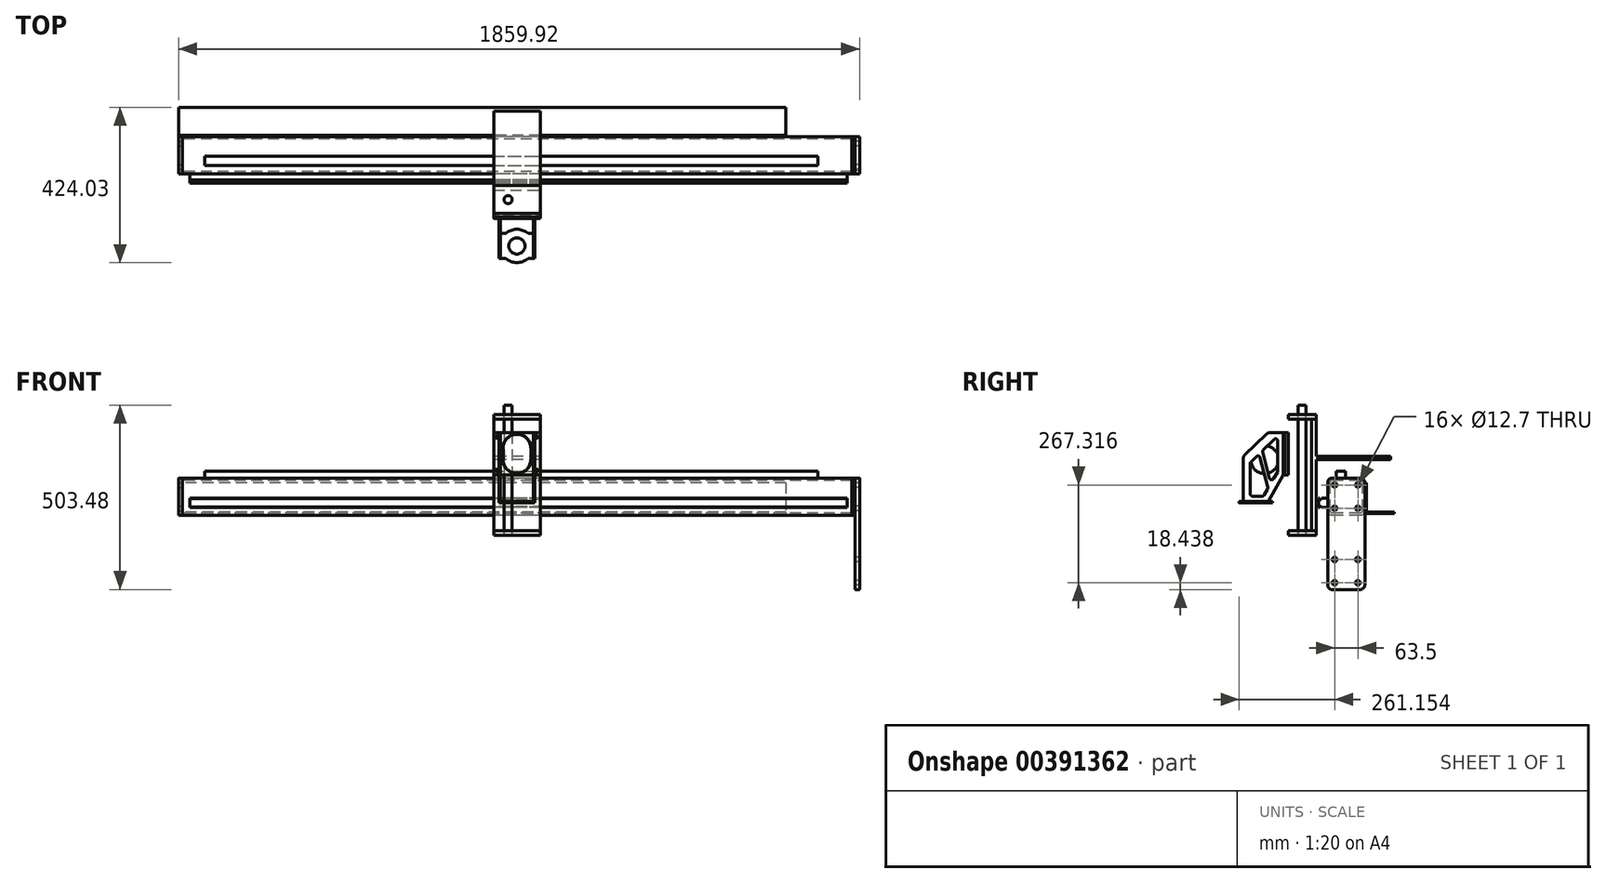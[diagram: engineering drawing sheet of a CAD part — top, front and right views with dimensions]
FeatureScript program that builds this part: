
annotation { "Feature Type Name" : "Feature", "Feature Type Description" : "" }
export const myFeature = defineFeature(function(context is Context, id is Id, definition is map)
    precondition{}
    {
        {
            var Q0;
            Q0=qCreatedBy(makeId("Right.planeOp"),FACE);
            var sketch = newSketch(context, id + "F0", { "sketchPlane" : qUnion([Q0])});
            skLineSegment(sketch, "E0.bottom", {"start": v(127.06, -109.78) * mm, "end": v(50.86, -109.78) * mm});
            skLineSegment(sketch, "E0.top", {"start": v(127.06, -8.18) * mm, "end": v(50.86, -8.18) * mm});
            skLineSegment(sketch, "E0.left", {"start": v(139.76, -97.08) * mm, "end": v(139.76, -20.88) * mm});
            skLineSegment(sketch, "E0.right", {"start": v(38.16, -97.08) * mm, "end": v(38.16, -20.88) * mm});
            skPoint(sketch, "E0.middle", {"position": v(88.96, -58.98) * mm});
            skPoint(sketch, "E1.visualSharp", {"position": v(38.16, -8.18) * mm});
            skArc(sketch, "E1.filletArc", {"start": v(50.86, -8.18) * mm, "mid": v(41.88, -11.9) * mm, "end": v(38.16, -20.88) * mm});
            skPoint(sketch, "E2.visualSharp", {"position": v(139.76, -8.18) * mm});
            skArc(sketch, "E2.filletArc", {"start": v(139.76, -20.88) * mm, "mid": v(136.04, -11.9) * mm, "end": v(127.06, -8.18) * mm});
            skPoint(sketch, "E3.visualSharp", {"position": v(139.76, -109.78) * mm});
            skArc(sketch, "E3.filletArc", {"start": v(127.06, -109.78) * mm, "mid": v(136.04, -106.06) * mm, "end": v(139.76, -97.08) * mm});
            skPoint(sketch, "E4.visualSharp", {"position": v(38.16, -109.78) * mm});
            skArc(sketch, "E4.filletArc", {"start": v(38.16, -97.08) * mm, "mid": v(41.88, -106.06) * mm, "end": v(50.86, -109.78) * mm});
            skArc(sketch, "E5.0", {"start": v(44.51, -97.08) * mm, "mid": v(46.37, -101.57) * mm, "end": v(50.86, -103.43) * mm});
            skLineSegment(sketch, "E5.1", {"start": v(127.06, -103.43) * mm, "end": v(50.86, -103.43) * mm});
            skLineSegment(sketch, "E5.2", {"start": v(44.51, -97.08) * mm, "end": v(44.51, -20.88) * mm});
            skArc(sketch, "E5.3", {"start": v(127.06, -103.43) * mm, "mid": v(131.55, -101.57) * mm, "end": v(133.41, -97.08) * mm});
            skArc(sketch, "E5.4", {"start": v(50.86, -14.53) * mm, "mid": v(46.37, -16.39) * mm, "end": v(44.51, -20.88) * mm});
            skLineSegment(sketch, "E5.5", {"start": v(127.06, -14.53) * mm, "end": v(50.86, -14.53) * mm});
            skArc(sketch, "E5.6", {"start": v(133.41, -20.88) * mm, "mid": v(131.55, -16.39) * mm, "end": v(127.06, -14.53) * mm});
            skLineSegment(sketch, "E5.7", {"start": v(133.41, -97.08) * mm, "end": v(133.41, -20.88) * mm});
            skSolve(sketch);
        }
        {
            var Q0;
            Q0=qCreatedBy(makeId("Top.planeOp"),FACE);
            var sketch = newSketch(context, id + "F1", { "sketchPlane" : qUnion([Q0])});
            skLineSegment(sketch, "E6.bottom", {"start": v(-63.5, -6.35) * mm, "end": v(63.5, -6.35) * mm});
            skLineSegment(sketch, "E6.top", {"start": v(-63.5, 6.35) * mm, "end": v(63.5, 6.35) * mm});
            skLineSegment(sketch, "E6.left", {"start": v(-63.5, -6.35) * mm, "end": v(-63.5, 6.35) * mm});
            skLineSegment(sketch, "E6.right", {"start": v(63.5, -6.35) * mm, "end": v(63.5, 6.35) * mm});
            skPoint(sketch, "E6.middle", {"position": v(0, 0) * mm});
            skSolve(sketch);
        }
        {
            var Q0;
            Q0 = qSketchRegion(id + "F1", true);
            extrude(context, id + "F2", {"entities" : qUnion([Q0]), "depth" : 304.8 * mm, "offsetDistance" : 25.4 * mm, "symmetric" : true});
        }
        {
            var Q0;
            Q0=makeQuery(id+"F2.opExtrude","CAP_FACE",FACE,{"disambiguationData":[OSD([sQuery(id+"F1.wireOp",EDGE,"E6.bottom"),sQuery(id+"F1.wireOp",EDGE,"E6.top"),sQuery(id+"F1.wireOp",EDGE,"E6.left"),sQuery(id+"F1.wireOp",EDGE,"E6.right")])],"isStart":false});
            var sketch = newSketch(context, id + "F3", { "sketchPlane" : qUnion([Q0])});
            skLineSegment(sketch, "E7.bottom", {"start": v(-63.5, 6.35) * mm, "end": v(63.5, 6.35) * mm});
            skLineSegment(sketch, "E7.top", {"start": v(-63.5, -69.85) * mm, "end": v(63.5, -69.85) * mm});
            skLineSegment(sketch, "E7.left", {"start": v(-63.5, 6.35) * mm, "end": v(-63.5, -69.85) * mm});
            skLineSegment(sketch, "E7.right", {"start": v(63.5, 6.35) * mm, "end": v(63.5, -69.85) * mm});
            skSolve(sketch);
        }
        {
            var Q0;
            Q0 = qSketchRegion(id + "F3", true);
            extrude(context, id + "F4", {"entities" : qUnion([Q0]), "depth" : 12.7 * mm, "offsetDistance" : 25.4 * mm});
        }
        {
            var Q0;
            Q0=makeQuery(id+"F2.opExtrude","CAP_FACE",FACE,{"disambiguationData":[OSD([sQuery(id+"F1.wireOp",EDGE,"E6.bottom"),sQuery(id+"F1.wireOp",EDGE,"E6.top"),sQuery(id+"F1.wireOp",EDGE,"E6.left"),sQuery(id+"F1.wireOp",EDGE,"E6.right")])],"isStart":true});
            var sketch = newSketch(context, id + "F5", { "sketchPlane" : qUnion([Q0])});
            skLineSegment(sketch, "E8.bottom", {"start": v(-63.5, -6.35) * mm, "end": v(63.5, -6.35) * mm});
            skLineSegment(sketch, "E8.top", {"start": v(-63.5, 69.85) * mm, "end": v(63.5, 69.85) * mm});
            skLineSegment(sketch, "E8.left", {"start": v(-63.5, -6.35) * mm, "end": v(-63.5, 69.85) * mm});
            skLineSegment(sketch, "E8.right", {"start": v(63.5, -6.35) * mm, "end": v(63.5, 69.85) * mm});
            skSolve(sketch);
        }
        {
            var Q0;
            {var subQ0=sQuery(id+"F5.wireOp",EDGE,"E8.top");Q0=makeQuery(id+"F5.imprint","IMPRINT",FACE,{"disambiguationData":[TD([[makeQuery(id+"F5.imprint","IMPRINT",EDGE,{"derivedFrom":subQ0}),-1.0]])]});}
            var Q1;
            {var subQ0=sQuery(id+"F5.wireOp",EDGE,"E8.bottom");Q1=makeQuery(id+"F5.imprint","IMPRINT",FACE,{"disambiguationData":[TD([[makeQuery(id+"F5.imprint","IMPRINT",EDGE,{"derivedFrom":subQ0}),1.0]])]});}
            extrude(context, id + "F6", {"entities" : qUnion([Q0, Q1]), "depth" : 12.7 * mm, "offsetDistance" : 25.4 * mm});
        }
        {
            var Q0;
            Q0=makeQuery(id+"F4.opExtrude","CAP_FACE",FACE,{"disambiguationData":[OSD([sQuery(id+"F3.wireOp",EDGE,"E7.bottom"),sQuery(id+"F3.wireOp",EDGE,"E7.top"),sQuery(id+"F3.wireOp",EDGE,"E7.left"),sQuery(id+"F3.wireOp",EDGE,"E7.right")])],"isStart":false});
            var sketch = newSketch(context, id + "F7", { "sketchPlane" : qUnion([Q0])});
            skCircle(sketch, "E9", {"center": v(-24.05, -31.75) * mm, "radius": 11.11 * mm});
            skPoint(sketch, "E9.centerSnap0", {"position": v(-63.5, -31.75) * mm});
            skSolve(sketch);
        }
        {
            var Q0;
            Q0 = qSketchRegion(id + "F7", true);
            extrude(context, id + "F8", {"entities" : qUnion([Q0]), "operationType" : NewBodyOperationType.REMOVE, "endBound" : BoundingType.THROUGH_ALL, "oppositeDirection" : true, "depth" : 25.4 * mm, "offsetDistance" : 25.4 * mm});
        }
        {
            var Q0;
            Q0=makeQuery(id+"F7.imprint","IMPRINT",FACE,{"disambiguationData":[TD([[makeQuery(id+"F7.imprint","IMPRINT",EDGE,{"derivedFrom":sQuery(id+"F7.wireOp",EDGE,"E9")}),1.0]])]});
            extrude(context, id + "F9", {"entities" : qUnion([Q0]), "depth" : 25.4 * mm, "offsetDistance" : 25.4 * mm, "hasSecondDirection" : true, "secondDirectionOppositeDirection" : true, "secondDirectionDepth" : 329.7 * mm});
        }
        {
            var Q0;
            Q0=makeQuery(id+"F4.opExtrude","SWEPT_FACE",FACE,{"disambiguationData":[OSD([sQuery(id+"F3.wireOp",EDGE,"E7.top")])]});
            var sketch = newSketch(context, id + "F10", { "sketchPlane" : qUnion([Q0])});
            skLineSegment(sketch, "E10.bottom", {"start": v(-63.5, 115.31) * mm, "end": v(63.5, 115.31) * mm});
            skLineSegment(sketch, "E10.top", {"start": v(-63.5, 0) * mm, "end": v(63.5, 0) * mm});
            skLineSegment(sketch, "E10.left", {"start": v(-63.5, 115.31) * mm, "end": v(-63.5, 0) * mm});
            skLineSegment(sketch, "E10.right", {"start": v(63.5, 115.31) * mm, "end": v(63.5, 0) * mm});
            skSolve(sketch);
        }
        {
            var Q0;
            Q0 = qSketchRegion(id + "F10", true);
            extrude(context, id + "F11", {"entities" : qUnion([Q0]), "depth" : 9.52 * mm, "offsetDistance" : 25.4 * mm});
        }
        {
            var Q0;
            Q0=makeQuery(id+"F11.opExtrude","CAP_FACE",FACE,{"disambiguationData":[OSD([sQuery(id+"F10.wireOp",EDGE,"E10.bottom"),sQuery(id+"F10.wireOp",EDGE,"E10.top"),sQuery(id+"F10.wireOp",EDGE,"E10.left"),sQuery(id+"F10.wireOp",EDGE,"E10.right")])],"isStart":false});
            var sketch = newSketch(context, id + "F12", { "sketchPlane" : qUnion([Q0])});
            skLineSegment(sketch, "E11", {"start": v(0, 72.63) * mm, "end": v(0, 42.69) * mm});
            skPoint(sketch, "E12", {"position": v(0, 57.66) * mm});
            skArc(sketch, "E13.0.startCap", {"start": v(-38.1, 72.63) * mm, "mid": v(0, 110.73) * mm, "end": v(38.1, 72.63) * mm});
            skArc(sketch, "E13.0.endCap", {"start": v(38.1, 42.69) * mm, "mid": v(0, 4.59) * mm, "end": v(-38.1, 42.69) * mm});
            skLineSegment(sketch, "E13.0.left", {"start": v(38.1, 72.63) * mm, "end": v(38.1, 42.69) * mm});
            skLineSegment(sketch, "E13.0.right", {"start": v(-38.1, 72.63) * mm, "end": v(-38.1, 42.69) * mm});
            skSolve(sketch);
        }
        {
            var Q0;
            Q0 = qSketchRegion(id + "F12", true);
            extrude(context, id + "F13", {"entities" : qUnion([Q0]), "operationType" : NewBodyOperationType.REMOVE, "oppositeDirection" : true, "depth" : 3.17 * mm, "offsetDistance" : 25.4 * mm});
        }
        {
            var Q0;
            Q0=makeQuery(id+"F11.opExtrude","CAP_FACE",FACE,{"disambiguationData":[OSD([sQuery(id+"F10.wireOp",EDGE,"E10.bottom"),sQuery(id+"F10.wireOp",EDGE,"E10.top"),sQuery(id+"F10.wireOp",EDGE,"E10.left"),sQuery(id+"F10.wireOp",EDGE,"E10.right")])],"isStart":false});
            var sketch = newSketch(context, id + "F14", { "sketchPlane" : qUnion([Q0])});
            skCircle(sketch, "E14", {"center": v(-55.13, 103.66) * mm, "radius": 3.18 * mm});
            skCircle(sketch, "E15", {"center": v(-55.13, 12.54) * mm, "radius": 3.18 * mm});
            skLineSegment(sketch, "E16", {"start": v(0, 115.31) * mm, "end": v(0, 0) * mm, "construction": true});
            skCircle(sketch, "E17.MirrorC", {"center": v(55.13, 103.66) * mm, "radius": 3.18 * mm});
            skCircle(sketch, "E18.MirrorC", {"center": v(55.13, 12.54) * mm, "radius": 3.18 * mm});
            skSolve(sketch);
        }
        {
            var Q0;
            Q0 = qSketchRegion(id + "F14", true);
            extrude(context, id + "F15", {"entities" : qUnion([Q0]), "operationType" : NewBodyOperationType.REMOVE, "oppositeDirection" : true, "depth" : 4.75 * mm, "offsetDistance" : 25.4 * mm});
        }
        {
            var Q0;
            Q0=makeQuery(id+"F11.opExtrude","CAP_FACE",FACE,{"disambiguationData":[OSD([sQuery(id+"F10.wireOp",EDGE,"E10.bottom"),sQuery(id+"F10.wireOp",EDGE,"E10.top"),sQuery(id+"F10.wireOp",EDGE,"E10.left"),sQuery(id+"F10.wireOp",EDGE,"E10.right")])],"isStart":false});
            var sketch = newSketch(context, id + "F16", { "sketchPlane" : qUnion([Q0])});
            skLineSegment(sketch, "E19.bottom", {"start": v(-61.01, 115.31) * mm, "end": v(0, 115.31) * mm});
            skLineSegment(sketch, "E19.top", {"start": v(-61.01, 0) * mm, "end": v(0, 0) * mm});
            skLineSegment(sketch, "E19.left", {"start": v(-63.5, 112.83) * mm, "end": v(-63.5, 2.49) * mm});
            skCircle(sketch, "E20.0", {"center": v(-55.13, 103.66) * mm, "radius": 3.17 * mm});
            skCircle(sketch, "E20.1", {"center": v(-55.13, 12.54) * mm, "radius": 3.17 * mm});
            skPoint(sketch, "E21.visualSharp", {"position": v(-44.45, 0) * mm});
            skPoint(sketch, "E22.visualSharp", {"position": v(-44.45, 115.31) * mm});
            skPoint(sketch, "E23.visualSharp", {"position": v(-63.5, 115.31) * mm});
            skArc(sketch, "E23.filletArc", {"start": v(-61.01, 115.31) * mm, "mid": v(-62.77, 114.58) * mm, "end": v(-63.5, 112.83) * mm});
            skPoint(sketch, "E24.visualSharp", {"position": v(-63.5, 0) * mm});
            skArc(sketch, "E24.filletArc", {"start": v(-63.5, 2.49) * mm, "mid": v(-62.77, 0.73) * mm, "end": v(-61.01, 0) * mm});
            skLineSegment(sketch, "E25", {"start": v(0, 115.31) * mm, "end": v(0, 0) * mm, "construction": true});
            skArc(sketch, "E26.MirrorCS", {"start": v(63.5, 2.49) * mm, "mid": v(62.77, 0.73) * mm, "end": v(61.01, 0) * mm});
            skArc(sketch, "E27.MirrorCS", {"start": v(61.01, 115.31) * mm, "mid": v(62.77, 114.58) * mm, "end": v(63.5, 112.83) * mm});
            skCircle(sketch, "E28.MirrorC", {"center": v(55.13, 103.66) * mm, "radius": 3.18 * mm});
            skCircle(sketch, "E29.MirrorC", {"center": v(55.13, 12.54) * mm, "radius": 3.18 * mm});
            skLineSegment(sketch, "E30.MirrorCS", {"start": v(61.01, 115.31) * mm, "end": v(0, 115.31) * mm});
            skPoint(sketch, "E31.MirrorP", {"position": v(63.5, 115.31) * mm});
            skLineSegment(sketch, "E32.MirrorCS", {"start": v(63.5, 112.83) * mm, "end": v(63.5, 2.49) * mm});
            skPoint(sketch, "E33.MirrorP", {"position": v(44.45, 115.31) * mm});
            skPoint(sketch, "E34.MirrorP", {"position": v(63.5, 0) * mm});
            skPoint(sketch, "E35.MirrorP", {"position": v(44.45, 0) * mm});
            skLineSegment(sketch, "E36.MirrorCS", {"start": v(61.01, 0) * mm, "end": v(0, 0) * mm});
            skLineSegment(sketch, "E37", {"start": v(-47.2, 23.12) * mm, "end": v(-47.2, 48.52) * mm, "construction": true});
            skLineSegment(sketch, "E38", {"start": v(-47.2, 68.54) * mm, "end": v(-47.2, 93.94) * mm, "construction": true});
            skPoint(sketch, "E39", {"position": v(-51.96, 103.66) * mm});
            skArc(sketch, "E40.0.startCap", {"start": v(-45.5, 68.54) * mm, "mid": v(-47.2, 66.83) * mm, "end": v(-48.92, 68.54) * mm});
            skArc(sketch, "E40.0.endCap", {"start": v(-48.92, 93.94) * mm, "mid": v(-47.2, 95.66) * mm, "end": v(-45.5, 93.94) * mm});
            skLineSegment(sketch, "E40.0.left", {"start": v(-48.92, 68.54) * mm, "end": v(-48.92, 93.94) * mm});
            skLineSegment(sketch, "E40.0.right", {"start": v(-45.5, 68.54) * mm, "end": v(-45.5, 93.94) * mm});
            skArc(sketch, "E40.1.startCap", {"start": v(-45.5, 23.12) * mm, "mid": v(-47.2, 21.4) * mm, "end": v(-48.92, 23.12) * mm});
            skArc(sketch, "E40.1.endCap", {"start": v(-48.92, 48.52) * mm, "mid": v(-47.2, 50.23) * mm, "end": v(-45.5, 48.52) * mm});
            skLineSegment(sketch, "E40.1.left", {"start": v(-48.92, 23.12) * mm, "end": v(-48.92, 48.52) * mm});
            skLineSegment(sketch, "E40.1.right", {"start": v(-45.5, 23.12) * mm, "end": v(-45.5, 48.52) * mm});
            skArc(sketch, "E41.MirrorCS", {"start": v(48.92, 48.52) * mm, "mid": v(47.2, 50.23) * mm, "end": v(45.5, 48.52) * mm});
            skArc(sketch, "E42.MirrorCS", {"start": v(45.5, 23.12) * mm, "mid": v(47.2, 21.4) * mm, "end": v(48.92, 23.12) * mm});
            skArc(sketch, "E43.MirrorCS", {"start": v(48.92, 93.94) * mm, "mid": v(47.2, 95.66) * mm, "end": v(45.5, 93.94) * mm});
            skArc(sketch, "E44.MirrorCS", {"start": v(45.5, 68.54) * mm, "mid": v(47.2, 66.83) * mm, "end": v(48.92, 68.54) * mm});
            skLineSegment(sketch, "E45.MirrorCS", {"start": v(45.5, 68.54) * mm, "end": v(45.5, 93.94) * mm});
            skLineSegment(sketch, "E46.MirrorCS", {"start": v(45.5, 23.12) * mm, "end": v(45.5, 48.52) * mm});
            skLineSegment(sketch, "E47.MirrorCS", {"start": v(48.92, 68.54) * mm, "end": v(48.92, 93.94) * mm});
            skLineSegment(sketch, "E48.MirrorCS", {"start": v(47.2, 68.54) * mm, "end": v(47.2, 93.94) * mm, "construction": true});
            skLineSegment(sketch, "E49.MirrorCS", {"start": v(47.2, 23.12) * mm, "end": v(47.2, 48.52) * mm, "construction": true});
            skLineSegment(sketch, "E50.MirrorCS", {"start": v(48.92, 23.12) * mm, "end": v(48.92, 48.52) * mm});
            skLineSegment(sketch, "E51.0", {"start": v(-38.1, 72.63) * mm, "end": v(-38.1, 42.69) * mm, "construction": true});
            skArc(sketch, "E51.1", {"start": v(38.1, 42.69) * mm, "mid": v(0, 4.59) * mm, "end": v(-38.1, 42.69) * mm, "construction": true});
            skLineSegment(sketch, "E51.2", {"start": v(38.1, 72.63) * mm, "end": v(38.1, 42.69) * mm, "construction": true});
            skArc(sketch, "E51.3", {"start": v(-38.1, 72.63) * mm, "mid": v(0, 110.73) * mm, "end": v(38.1, 72.63) * mm, "construction": true});
            skArc(sketch, "E52.0", {"start": v(-38.89, 72.63) * mm, "mid": v(0, 111.51) * mm, "end": v(38.89, 72.63) * mm});
            skLineSegment(sketch, "E52.1", {"start": v(-38.89, 72.63) * mm, "end": v(-38.89, 42.69) * mm});
            skArc(sketch, "E52.2", {"start": v(38.89, 42.69) * mm, "mid": v(0, 3.8) * mm, "end": v(-38.89, 42.69) * mm});
            skLineSegment(sketch, "E52.3", {"start": v(38.89, 72.63) * mm, "end": v(38.89, 42.69) * mm});
            skSolve(sketch);
        }
        {
            var Q0;
            Q0 = qSketchRegion(id + "F16", true);
            extrude(context, id + "F17", {"entities" : qUnion([Q0]), "depth" : 3.43 * mm, "offsetDistance" : 25.4 * mm});
        }
        {
            var Q0;
            Q0=makeQuery(id+"F17.opExtrude","SWEPT_FACE",FACE,{"disambiguationData":[OSD([sQuery(id+"F16.wireOp",EDGE,"E50.MirrorCS")])]});
            var sketch = newSketch(context, id + "F18", { "sketchPlane" : qUnion([Q0])});
            skLineSegment(sketch, "E53", {"start": v(82.8, 93.94) * mm, "end": v(82.8, 115.31) * mm});
            skLineSegment(sketch, "E54", {"start": v(82.8, 48.52) * mm, "end": v(82.8, 68.54) * mm});
            skLineSegment(sketch, "E55", {"start": v(82.8, 0) * mm, "end": v(82.8, 23.12) * mm});
            skLineSegment(sketch, "E56.0", {"start": v(82.8, 48.52) * mm, "end": v(79.38, 48.52) * mm});
            skLineSegment(sketch, "E56.1", {"start": v(79.38, 23.12) * mm, "end": v(79.38, 48.52) * mm});
            skLineSegment(sketch, "E56.2", {"start": v(82.8, 23.12) * mm, "end": v(79.38, 23.12) * mm});
            skLineSegment(sketch, "E56.3", {"start": v(82.8, 93.94) * mm, "end": v(79.38, 93.94) * mm});
            skLineSegment(sketch, "E56.4", {"start": v(79.38, 68.54) * mm, "end": v(79.38, 93.94) * mm});
            skLineSegment(sketch, "E56.5", {"start": v(82.8, 68.54) * mm, "end": v(79.38, 68.54) * mm});
            skLineSegment(sketch, "E57", {"start": v(82.8, 115.31) * mm, "end": v(120.62, 115.31) * mm});
            skLineSegment(sketch, "E58", {"start": v(129.47, 111.71) * mm, "end": v(188.47, 54.3) * mm});
            skLineSegment(sketch, "E59", {"start": v(192.3, 45.2) * mm, "end": v(192.3, -71.7) * mm});
            skLineSegment(sketch, "E60", {"start": v(192.3, -71.7) * mm, "end": v(124.58, -71.7) * mm});
            skLineSegment(sketch, "E61", {"start": v(124.58, -71.7) * mm, "end": v(82.8, 0) * mm});
            skPoint(sketch, "E62.visualSharp", {"position": v(125.78, 115.31) * mm});
            skArc(sketch, "E62.filletArc", {"start": v(129.47, 111.71) * mm, "mid": v(125.4, 114.38) * mm, "end": v(120.62, 115.31) * mm});
            skPoint(sketch, "E63.visualSharp", {"position": v(192.3, 50.55) * mm});
            skArc(sketch, "E63.filletArc", {"start": v(192.3, 45.2) * mm, "mid": v(191.3, 50.13) * mm, "end": v(188.47, 54.3) * mm});
            skLineSegment(sketch, "E64", {"start": v(97.93, 92.4) * mm, "end": v(97.93, 11.3) * mm});
            skLineSegment(sketch, "E65", {"start": v(98.8, 8.1) * mm, "end": v(109.39, -10.07) * mm});
            skLineSegment(sketch, "E66", {"start": v(141.09, -58.2) * mm, "end": v(167.03, -58.2) * mm});
            skLineSegment(sketch, "E67", {"start": v(173.38, -51.85) * mm, "end": v(173.38, 31.32) * mm});
            skLineSegment(sketch, "E68", {"start": v(171.46, 35.87) * mm, "end": v(156.89, 50.05) * mm});
            skPoint(sketch, "E69.visualSharp", {"position": v(97.93, 107.43) * mm});
            skArc(sketch, "E69.filletArc", {"start": v(108.71, 96.94) * mm, "mid": v(101.82, 98.24) * mm, "end": v(97.93, 92.4) * mm});
            skPoint(sketch, "E70.visualSharp", {"position": v(97.93, 9.59) * mm});
            skArc(sketch, "E70.filletArc", {"start": v(97.93, 11.3) * mm, "mid": v(98.15, 9.65) * mm, "end": v(98.8, 8.1) * mm});
            skPoint(sketch, "E71.visualSharp", {"position": v(173.38, -58.2) * mm});
            skArc(sketch, "E71.filletArc", {"start": v(167.03, -58.2) * mm, "mid": v(171.52, -56.34) * mm, "end": v(173.38, -51.85) * mm});
            skPoint(sketch, "E72.visualSharp", {"position": v(173.38, 34) * mm});
            skArc(sketch, "E72.filletArc", {"start": v(173.38, 31.32) * mm, "mid": v(172.88, 33.79) * mm, "end": v(171.46, 35.87) * mm});
            skPoint(sketch, "E73.visualSharp", {"position": v(137.44, -58.2) * mm});
            skArc(sketch, "E73.filletArc", {"start": v(135.6, -55.05) * mm, "mid": v(137.92, -57.36) * mm, "end": v(141.09, -58.2) * mm});
            skLineSegment(sketch, "E74", {"start": v(121.03, -8.44) * mm, "end": v(139.18, 62.85) * mm});
            skLineSegment(sketch, "E75", {"start": v(146.3, 47.07) * mm, "end": v(125.6, -34.26) * mm});
            skLineSegment(sketch, "E76.trimOffspring", {"start": v(137.45, 68.96) * mm, "end": v(108.71, 96.94) * mm});
            skLineSegment(sketch, "E77.trimOffspring", {"start": v(126.26, -39.03) * mm, "end": v(135.6, -55.05) * mm});
            skPoint(sketch, "E78.visualSharp", {"position": v(149.02, 57.71) * mm});
            skArc(sketch, "E78.filletArc", {"start": v(156.89, 50.05) * mm, "mid": v(150.74, 51.61) * mm, "end": v(146.3, 47.07) * mm});
            skPoint(sketch, "E79.visualSharp", {"position": v(124.96, -36.78) * mm});
            skArc(sketch, "E79.filletArc", {"start": v(125.6, -34.26) * mm, "mid": v(125.46, -36.71) * mm, "end": v(126.26, -39.03) * mm});
            skPoint(sketch, "E80.visualSharp", {"position": v(140.09, 66.4) * mm});
            skArc(sketch, "E80.filletArc", {"start": v(139.18, 62.85) * mm, "mid": v(139.14, 66.14) * mm, "end": v(137.45, 68.96) * mm});
            skPoint(sketch, "E81.visualSharp", {"position": v(117.2, -23.47) * mm});
            skArc(sketch, "E81.filletArc", {"start": v(109.39, -10.07) * mm, "mid": v(115.75, -13.16) * mm, "end": v(121.03, -8.44) * mm});
            skSolve(sketch);
        }
        {
            var Q0;
            Q0 = qSketchRegion(id + "F18", true);
            extrude(context, id + "F19", {"entities" : qUnion([Q0]), "depth" : 3.43 * mm, "offsetDistance" : 25.4 * mm});
        }
        {
            var Q0;
            Q0=makeQuery(id+"F19.opExtrude","SWEPT_BODY",BODY,{"disambiguationData":[OSD([sQuery(id+"F18.wireOp",EDGE,"E53"),sQuery(id+"F18.wireOp",EDGE,"E54"),sQuery(id+"F18.wireOp",EDGE,"E55"),sQuery(id+"F18.wireOp",EDGE,"E56.0"),sQuery(id+"F18.wireOp",EDGE,"E56.1"),sQuery(id+"F18.wireOp",EDGE,"E56.2"),sQuery(id+"F18.wireOp",EDGE,"E56.3"),sQuery(id+"F18.wireOp",EDGE,"E56.4"),sQuery(id+"F18.wireOp",EDGE,"E56.5"),sQuery(id+"F18.wireOp",EDGE,"E57"),sQuery(id+"F18.wireOp",EDGE,"E58"),sQuery(id+"F18.wireOp",EDGE,"E59"),sQuery(id+"F18.wireOp",EDGE,"E60"),sQuery(id+"F18.wireOp",EDGE,"E61"),sQuery(id+"F18.wireOp",EDGE,"E62.filletArc"),sQuery(id+"F18.wireOp",EDGE,"E63.filletArc"),sQuery(id+"F18.wireOp",EDGE,"E64"),sQuery(id+"F18.wireOp",EDGE,"E65"),sQuery(id+"F18.wireOp",EDGE,"E66"),sQuery(id+"F18.wireOp",EDGE,"E67"),sQuery(id+"F18.wireOp",EDGE,"E68"),sQuery(id+"F18.wireOp",EDGE,"E69.filletArc"),sQuery(id+"F18.wireOp",EDGE,"E70.filletArc"),sQuery(id+"F18.wireOp",EDGE,"E71.filletArc"),sQuery(id+"F18.wireOp",EDGE,"E72.filletArc"),sQuery(id+"F18.wireOp",EDGE,"E73.filletArc"),sQuery(id+"F18.wireOp",EDGE,"E74"),sQuery(id+"F18.wireOp",EDGE,"E75"),sQuery(id+"F18.wireOp",EDGE,"E76.trimOffspring"),sQuery(id+"F18.wireOp",EDGE,"E77.trimOffspring"),sQuery(id+"F18.wireOp",EDGE,"E78.filletArc"),sQuery(id+"F18.wireOp",EDGE,"E79.filletArc"),sQuery(id+"F18.wireOp",EDGE,"E80.filletArc"),sQuery(id+"F18.wireOp",EDGE,"E81.filletArc")])]});
            var Q1;
            Q1=qCreatedBy(makeId("Right.planeOp"),FACE);
            mirror(context, id + "F20", {"entities" : qUnion([Q0]), "mirrorPlane" : qUnion([Q1])});
        }
        {
            var Q0;
            Q0=makeQuery(id+"F19.opExtrude","SWEPT_FACE",FACE,{"disambiguationData":[OSD([sQuery(id+"F18.wireOp",EDGE,"E60")])]});
            var sketch = newSketch(context, id + "F21", { "sketchPlane" : qUnion([Q0])});
            skLineSegment(sketch, "E82.bottom", {"start": v(48.92, 192.3) * mm, "end": v(30.38, 192.3) * mm});
            skLineSegment(sketch, "E82.top", {"start": v(48.92, 124.58) * mm, "end": v(30.38, 124.58) * mm});
            skLineSegment(sketch, "E82.left", {"start": v(48.92, 192.3) * mm, "end": v(48.92, 124.58) * mm});
            skLineSegment(sketch, "E82.right", {"start": v(-48.92, 192.3) * mm, "end": v(-48.92, 124.58) * mm});
            skArc(sketch, "E83", {"start": v(30.38, 192.3) * mm, "mid": v(0, 203.94) * mm, "end": v(-30.38, 192.3) * mm});
            skPoint(sketch, "E83.centerSnap0", {"position": v(45.5, 158.45) * mm});
            skArc(sketch, "E84.trimOffspring", {"start": v(-30.38, 124.58) * mm, "mid": v(0, 112.95) * mm, "end": v(30.38, 124.58) * mm});
            skLineSegment(sketch, "E85.trimOffspring", {"start": v(-30.38, 192.3) * mm, "end": v(-48.92, 192.3) * mm});
            skLineSegment(sketch, "E86.trimOffspring", {"start": v(-30.38, 124.58) * mm, "end": v(-48.92, 124.58) * mm});
            skSolve(sketch);
        }
        {
            var Q0;
            Q0 = qSketchRegion(id + "F21", true);
            extrude(context, id + "F22", {"entities" : qUnion([Q0]), "depth" : 4.75 * mm, "offsetDistance" : 25.4 * mm});
        }
        {
            var Q0;
            Q0=makeQuery(id+"F22.opExtrude","CAP_FACE",FACE,{"disambiguationData":[OSD([sQuery(id+"F21.wireOp",EDGE,"E82.bottom"),sQuery(id+"F21.wireOp",EDGE,"E82.top"),sQuery(id+"F21.wireOp",EDGE,"E82.left"),sQuery(id+"F21.wireOp",EDGE,"E82.right")])],"isStart":true});
            var sketch = newSketch(context, id + "F23", { "sketchPlane" : qUnion([Q0])});
            skCircle(sketch, "E87", {"center": v(0, -158.45) * mm, "radius": 22.23 * mm});
            skPoint(sketch, "E87.centerSnap1", {"position": v(48.92, -158.45) * mm});
            skSolve(sketch);
        }
        {
            var Q0;
            Q0=makeQuery(id+"F23.imprint","IMPRINT",FACE,{"disambiguationData":[TD([[makeQuery(id+"F23.imprint","IMPRINT",EDGE,{"derivedFrom":sQuery(id+"F23.wireOp",EDGE,"E87")}),1.0]])]});
            extrude(context, id + "F24", {"entities" : qUnion([Q0]), "operationType" : NewBodyOperationType.REMOVE, "oppositeDirection" : true, "depth" : 25.4 * mm, "offsetDistance" : 25.4 * mm});
        }
        {
            var Q0;
            Q0=makeQuery(id+"F2.opExtrude","SWEPT_FACE",FACE,{"disambiguationData":[OSD([sQuery(id+"F1.wireOp",EDGE,"E6.top")])]});
            var sketch = newSketch(context, id + "F25", { "sketchPlane" : qUnion([Q0])});
            skLineSegment(sketch, "E88.bottom", {"start": v(-63.5, 51) * mm, "end": v(63.5, 51) * mm});
            skLineSegment(sketch, "E88.top", {"start": v(-63.5, 41.47) * mm, "end": v(63.5, 41.47) * mm});
            skLineSegment(sketch, "E88.left", {"start": v(-63.5, 51) * mm, "end": v(-63.5, 41.47) * mm});
            skLineSegment(sketch, "E88.right", {"start": v(63.5, 51) * mm, "end": v(63.5, 41.47) * mm});
            skSolve(sketch);
        }
        {
            var Q0;
            Q0 = qSketchRegion(id + "F25", true);
            extrude(context, id + "F26", {"entities" : qUnion([Q0]), "operationType" : NewBodyOperationType.ADD, "depth" : 203.2 * mm, "offsetDistance" : 25.4 * mm});
        }
        {
            var Q0;
            Q0=makeQuery(id+"F0.imprint","IMPRINT",FACE,{"disambiguationData":[TD([[makeQuery(id+"F0.imprint","IMPRINT",EDGE,{"derivedFrom":sQuery(id+"F0.wireOp",EDGE,"E0.bottom")}),-1.0]])]});
            extrude(context, id + "F27", {"entities" : qUnion([Q0]), "depth" : 1828.8 * mm, "offsetDistance" : 25.4 * mm, "symmetric" : true});
        }
        {
            var Q0;
            Q0=makeQuery(id+"F27.opExtrude","CAP_FACE",FACE,{"disambiguationData":[OSD([sQuery(id+"F0.wireOp",EDGE,"E0.bottom"),sQuery(id+"F0.wireOp",EDGE,"E0.top"),sQuery(id+"F0.wireOp",EDGE,"E0.left"),sQuery(id+"F0.wireOp",EDGE,"E0.right"),sQuery(id+"F0.wireOp",EDGE,"E1.filletArc"),sQuery(id+"F0.wireOp",EDGE,"E2.filletArc"),sQuery(id+"F0.wireOp",EDGE,"E3.filletArc"),sQuery(id+"F0.wireOp",EDGE,"E4.filletArc"),sQuery(id+"F0.wireOp",EDGE,"E5.0"),sQuery(id+"F0.wireOp",EDGE,"E5.1"),sQuery(id+"F0.wireOp",EDGE,"E5.2"),sQuery(id+"F0.wireOp",EDGE,"E5.3"),sQuery(id+"F0.wireOp",EDGE,"E5.4"),sQuery(id+"F0.wireOp",EDGE,"E5.5"),sQuery(id+"F0.wireOp",EDGE,"E5.6"),sQuery(id+"F0.wireOp",EDGE,"E5.7")])],"isStart":false});
            var sketch = newSketch(context, id + "F28", { "sketchPlane" : qUnion([Q0])});
            skLineSegment(sketch, "E89.0", {"start": v(127.06, -109.78) * mm, "end": v(50.86, -109.78) * mm});
            skArc(sketch, "E89.1", {"start": v(127.06, -109.78) * mm, "mid": v(136.04, -106.06) * mm, "end": v(139.76, -97.08) * mm});
            skLineSegment(sketch, "E89.2", {"start": v(139.76, -97.08) * mm, "end": v(139.76, -20.88) * mm});
            skArc(sketch, "E89.3", {"start": v(139.76, -20.88) * mm, "mid": v(136.04, -11.9) * mm, "end": v(127.06, -8.18) * mm});
            skLineSegment(sketch, "E89.4", {"start": v(127.06, -8.18) * mm, "end": v(50.86, -8.18) * mm});
            skArc(sketch, "E89.5", {"start": v(50.86, -8.18) * mm, "mid": v(41.88, -11.9) * mm, "end": v(38.16, -20.88) * mm});
            skLineSegment(sketch, "E89.6", {"start": v(38.16, -97.08) * mm, "end": v(38.16, -20.88) * mm});
            skArc(sketch, "E89.7", {"start": v(38.16, -97.08) * mm, "mid": v(41.88, -106.06) * mm, "end": v(50.86, -109.78) * mm});
            skCircle(sketch, "E90", {"center": v(57.21, -27.23) * mm, "radius": 6.35 * mm});
            skCircle(sketch, "E91.0.1.0", {"center": v(57.21, -90.73) * mm, "radius": 6.35 * mm});
            skCircle(sketch, "E91.1.0.0", {"center": v(120.71, -27.23) * mm, "radius": 6.35 * mm});
            skCircle(sketch, "E91.1.1.0", {"center": v(120.71, -90.73) * mm, "radius": 6.35 * mm});
            skLineSegment(sketch, "E91.direction1", {"start": v(57.21, -27.23) * mm, "end": v(120.71, -27.23) * mm, "construction": true});
            skLineSegment(sketch, "E91.direction2", {"start": v(57.21, -27.23) * mm, "end": v(57.21, -90.73) * mm, "construction": true});
            skLineSegment(sketch, "E92", {"start": v(50.86, -20.88) * mm, "end": v(127.06, -20.88) * mm, "construction": true});
            skLineSegment(sketch, "E93", {"start": v(127.06, -97.08) * mm, "end": v(127.06, -20.88) * mm, "construction": true});
            skLineSegment(sketch, "E94", {"start": v(50.86, -20.88) * mm, "end": v(50.86, -97.08) * mm, "construction": true});
            skLineSegment(sketch, "E95", {"start": v(50.86, -97.08) * mm, "end": v(127.06, -97.08) * mm, "construction": true});
            skSolve(sketch);
        }
        {
            var Q0;
            Q0 = qSketchRegion(id + "F28", true);
            extrude(context, id + "F29", {"entities" : qUnion([Q0]), "depth" : 9.52 * mm, "offsetDistance" : 25.4 * mm});
        }
        {
            var Q0;
            Q0=makeQuery(id+"F29.opExtrude","SWEPT_BODY",BODY,{"disambiguationData":[OSD([sQuery(id+"F28.wireOp",EDGE,"E89.0"),sQuery(id+"F28.wireOp",EDGE,"E89.1"),sQuery(id+"F28.wireOp",EDGE,"E89.2"),sQuery(id+"F28.wireOp",EDGE,"E89.3"),sQuery(id+"F28.wireOp",EDGE,"E89.4"),sQuery(id+"F28.wireOp",EDGE,"E89.5"),sQuery(id+"F28.wireOp",EDGE,"E89.6"),sQuery(id+"F28.wireOp",EDGE,"E89.7"),sQuery(id+"F28.wireOp",EDGE,"E90"),sQuery(id+"F28.wireOp",EDGE,"E91.0.1.0"),sQuery(id+"F28.wireOp",EDGE,"E91.1.0.0"),sQuery(id+"F28.wireOp",EDGE,"E91.1.1.0")])]});
            var Q1;
            Q1=qCreatedBy(makeId("Right.planeOp"),FACE);
            mirror(context, id + "F30", {"entities" : qUnion([Q0]), "mirrorPlane" : qUnion([Q1])});
        }
        {
            var Q0;
            Q0=makeQuery(id+"F27.opExtrude","SWEPT_FACE",FACE,{"disambiguationData":[OSD([sQuery(id+"F0.wireOp",EDGE,"E0.top")])]});
            var sketch = newSketch(context, id + "F31", { "sketchPlane" : qUnion([Q0])});
            skLineSegment(sketch, "E96.bottom", {"start": v(-852.94, 61.67) * mm, "end": v(821.66, 61.67) * mm});
            skLineSegment(sketch, "E96.top", {"start": v(-852.94, 87.07) * mm, "end": v(821.66, 87.07) * mm});
            skLineSegment(sketch, "E96.left", {"start": v(-852.94, 61.67) * mm, "end": v(-852.94, 87.07) * mm});
            skLineSegment(sketch, "E96.right", {"start": v(821.66, 61.67) * mm, "end": v(821.66, 87.07) * mm});
            skSolve(sketch);
        }
        {
            var Q0;
            Q0 = qSketchRegion(id + "F31", true);
            extrude(context, id + "F32", {"entities" : qUnion([Q0]), "depth" : 19.05 * mm, "offsetDistance" : 25.4 * mm});
        }
        {
            var Q0;
            Q0=makeQuery(id+"F27.opExtrude","SWEPT_FACE",FACE,{"disambiguationData":[OSD([sQuery(id+"F0.wireOp",EDGE,"E0.right")])]});
            var sketch = newSketch(context, id + "F33", { "sketchPlane" : qUnion([Q0])});
            skLineSegment(sketch, "E97.bottom", {"start": v(-893.56, -63.9) * mm, "end": v(902.34, -63.9) * mm});
            skLineSegment(sketch, "E97.top", {"start": v(-893.56, -89.3) * mm, "end": v(902.34, -89.3) * mm});
            skLineSegment(sketch, "E97.left", {"start": v(-893.56, -63.9) * mm, "end": v(-893.56, -89.3) * mm});
            skLineSegment(sketch, "E97.right", {"start": v(902.34, -63.9) * mm, "end": v(902.34, -89.3) * mm});
            skSolve(sketch);
        }
        {
            var Q0;
            Q0 = qSketchRegion(id + "F33", true);
            extrude(context, id + "F34", {"entities" : qUnion([Q0]), "depth" : 25.4 * mm, "offsetDistance" : 25.4 * mm});
        }
        {
            var Q0;
            Q0=makeQuery(id+"F34.opExtrude","SWEPT_FACE",FACE,{"disambiguationData":[OSD([sQuery(id+"F33.wireOp",EDGE,"E97.left")])]});
            var sketch = newSketch(context, id + "F35", { "sketchPlane" : qUnion([Q0])});
            skLineSegment(sketch, "E98", {"start": v(-22.1, -63.9) * mm, "end": v(-20.52, -66.75) * mm});
            skLineSegment(sketch, "E99", {"start": v(-20.52, -66.75) * mm, "end": v(-17.5, -66.75) * mm});
            skLineSegment(sketch, "E100", {"start": v(-17.5, -66.75) * mm, "end": v(-15.19, -63.9) * mm});
            skLineSegment(sketch, "E101", {"start": v(-15.19, -63.9) * mm, "end": v(-13.74, -63.9) * mm});
            skLineSegment(sketch, "E102", {"start": v(-13.74, -63.9) * mm, "end": v(-12.76, -65.02) * mm});
            skLineSegment(sketch, "E103", {"start": v(-12.76, -65.02) * mm, "end": v(-12.76, -76.6) * mm});
            skLineSegment(sketch, "E104", {"start": v(-22.1, -63.9) * mm, "end": v(-38.16, -63.9) * mm});
            skLineSegment(sketch, "E105", {"start": v(-12.76, -76.6) * mm, "end": v(-38.16, -76.6) * mm, "construction": true});
            skLineSegment(sketch, "E106", {"start": v(-38.16, -63.9) * mm, "end": v(-38.16, -76.6) * mm});
            skLineSegment(sketch, "E107.MirrorCS", {"start": v(-12.76, -88.17) * mm, "end": v(-12.76, -76.6) * mm});
            skLineSegment(sketch, "E108.MirrorCS", {"start": v(-15.19, -89.3) * mm, "end": v(-13.74, -89.3) * mm});
            skLineSegment(sketch, "E109.MirrorCS", {"start": v(-13.74, -89.3) * mm, "end": v(-12.76, -88.17) * mm});
            skLineSegment(sketch, "E110.MirrorCS", {"start": v(-17.5, -86.44) * mm, "end": v(-15.19, -89.3) * mm});
            skLineSegment(sketch, "E111.MirrorCS", {"start": v(-20.52, -86.44) * mm, "end": v(-17.5, -86.44) * mm});
            skLineSegment(sketch, "E112.MirrorCS", {"start": v(-22.1, -89.3) * mm, "end": v(-20.52, -86.44) * mm});
            skLineSegment(sketch, "E113.MirrorCS", {"start": v(-22.1, -89.3) * mm, "end": v(-38.16, -89.3) * mm});
            skLineSegment(sketch, "E114.MirrorCS", {"start": v(-38.16, -89.3) * mm, "end": v(-38.16, -76.6) * mm});
            skSolve(sketch);
        }
        {
            var Q0;
            {var subQ0=sQuery(id+"F35.wireOp",EDGE,"E110.MirrorCS");Q0=makeQuery(id+"F35.imprint","IMPRINT",FACE,{"disambiguationData":[TD([[makeQuery(id+"F35.imprint","IMPRINT",EDGE,{"derivedFrom":subQ0}),-1.0]])]});}
            var Q1;
            {var subQ0=sQuery(id+"F35.wireOp",EDGE,"E109.MirrorCS");Q1=makeQuery(id+"F35.imprint","IMPRINT",FACE,{"disambiguationData":[TD([[makeQuery(id+"F35.imprint","IMPRINT",EDGE,{"derivedFrom":subQ0}),-1.0]])]});}
            var Q2;
            {var subQ0=sQuery(id+"F35.wireOp",EDGE,"E98");Q2=makeQuery(id+"F35.imprint","IMPRINT",FACE,{"disambiguationData":[TD([[makeQuery(id+"F35.imprint","IMPRINT",EDGE,{"derivedFrom":subQ0}),1.0]])]});}
            var Q3;
            {var subQ0=sQuery(id+"F35.wireOp",EDGE,"E102");Q3=makeQuery(id+"F35.imprint","IMPRINT",FACE,{"disambiguationData":[TD([[makeQuery(id+"F35.imprint","IMPRINT",EDGE,{"derivedFrom":subQ0}),1.0]])]});}
            extrude(context, id + "F36", {"entities" : qUnion([Q0, Q1, Q2, Q3]), "operationType" : NewBodyOperationType.REMOVE, "endBound" : BoundingType.THROUGH_ALL, "oppositeDirection" : true, "depth" : 25.4 * mm, "offsetDistance" : 25.4 * mm});
        }
        {
            var Q0;
            Q0=makeQuery(id+"F30.opPattern","COPY",FACE,{"derivedFrom":makeQuery(id+"F29.opExtrude","CAP_FACE",FACE,{"disambiguationData":[OSD([sQuery(id+"F28.wireOp",EDGE,"E89.0"),sQuery(id+"F28.wireOp",EDGE,"E89.1"),sQuery(id+"F28.wireOp",EDGE,"E89.2"),sQuery(id+"F28.wireOp",EDGE,"E89.3"),sQuery(id+"F28.wireOp",EDGE,"E89.4"),sQuery(id+"F28.wireOp",EDGE,"E89.5"),sQuery(id+"F28.wireOp",EDGE,"E89.6"),sQuery(id+"F28.wireOp",EDGE,"E89.7"),sQuery(id+"F28.wireOp",EDGE,"E90"),sQuery(id+"F28.wireOp",EDGE,"E91.0.1.0"),sQuery(id+"F28.wireOp",EDGE,"E91.1.0.0"),sQuery(id+"F28.wireOp",EDGE,"E91.1.1.0")])],"isStart":false}),"instanceName":"1"});
            var sketch = newSketch(context, id + "F37", { "sketchPlane" : qUnion([Q0])});
            skLineSegment(sketch, "E115.bottom", {"start": v(-139.76, -20.88) * mm, "end": v(-144.51, -20.88) * mm});
            skLineSegment(sketch, "E115.top", {"start": v(-139.76, -101.2) * mm, "end": v(-144.51, -101.2) * mm});
            skLineSegment(sketch, "E115.left", {"start": v(-139.76, -20.88) * mm, "end": v(-139.76, -101.2) * mm});
            skLineSegment(sketch, "E115.right", {"start": v(-144.51, -20.88) * mm, "end": v(-144.51, -101.2) * mm});
            skLineSegment(sketch, "E116.bottom", {"start": v(-139.76, -101.2) * mm, "end": v(-220.09, -101.2) * mm});
            skLineSegment(sketch, "E116.top", {"start": v(-139.76, -105.95) * mm, "end": v(-220.09, -105.95) * mm});
            skLineSegment(sketch, "E116.left", {"start": v(-139.76, -101.2) * mm, "end": v(-139.76, -105.95) * mm});
            skLineSegment(sketch, "E116.right", {"start": v(-220.09, -101.2) * mm, "end": v(-220.09, -105.95) * mm});
            skSolve(sketch);
        }
        {
            var Q0;
            Q0 = qSketchRegion(id + "F37", true);
            extrude(context, id + "F38", {"entities" : qUnion([Q0]), "oppositeDirection" : true, "depth" : 1658.62 * mm, "offsetDistance" : 25.4 * mm});
        }
        {
            var Q0;
            Q0=makeQuery(id+"F29.opExtrude","CAP_FACE",FACE,{"disambiguationData":[OSD([sQuery(id+"F28.wireOp",EDGE,"E89.0"),sQuery(id+"F28.wireOp",EDGE,"E89.1"),sQuery(id+"F28.wireOp",EDGE,"E89.2"),sQuery(id+"F28.wireOp",EDGE,"E89.3"),sQuery(id+"F28.wireOp",EDGE,"E89.4"),sQuery(id+"F28.wireOp",EDGE,"E89.5"),sQuery(id+"F28.wireOp",EDGE,"E89.6"),sQuery(id+"F28.wireOp",EDGE,"E89.7"),sQuery(id+"F28.wireOp",EDGE,"E90"),sQuery(id+"F28.wireOp",EDGE,"E91.0.1.0"),sQuery(id+"F28.wireOp",EDGE,"E91.1.0.0"),sQuery(id+"F28.wireOp",EDGE,"E91.1.1.0")])],"isStart":false});
            var sketch = newSketch(context, id + "F39", { "sketchPlane" : qUnion([Q0])});
            skCircle(sketch, "E117", {"center": v(120.71, -27.23) * mm, "radius": 6.35 * mm});
            skCircle(sketch, "E118", {"center": v(57.21, -90.73) * mm, "radius": 6.35 * mm});
            skCircle(sketch, "E119", {"center": v(57.21, -27.23) * mm, "radius": 6.35 * mm});
            skLineSegment(sketch, "E120", {"start": v(139.76, -300.37) * mm, "end": v(139.76, -20.88) * mm});
            skArc(sketch, "E121", {"start": v(128.6, -312.98) * mm, "mid": v(136.57, -308.79) * mm, "end": v(139.76, -300.37) * mm});
            skLineSegment(sketch, "E122", {"start": v(128.6, -312.98) * mm, "end": v(46.96, -312.98) * mm});
            skArc(sketch, "E123", {"start": v(38.16, -300.9) * mm, "mid": v(40.6, -308.36) * mm, "end": v(46.96, -312.98) * mm});
            skLineSegment(sketch, "E124", {"start": v(38.16, -300.9) * mm, "end": v(38.16, -20.88) * mm});
            skArc(sketch, "E125", {"start": v(50.86, -8.18) * mm, "mid": v(41.88, -11.9) * mm, "end": v(38.16, -20.88) * mm});
            skLineSegment(sketch, "E126", {"start": v(127.06, -8.18) * mm, "end": v(50.86, -8.18) * mm});
            skArc(sketch, "E127", {"start": v(139.76, -20.88) * mm, "mid": v(136.04, -11.9) * mm, "end": v(127.06, -8.18) * mm});
            skCircle(sketch, "E128", {"center": v(120.71, -90.73) * mm, "radius": 6.35 * mm});
            skLineSegment(sketch, "E129", {"start": v(38.16, -160.88) * mm, "end": v(139.76, -160.88) * mm, "construction": true});
            skCircle(sketch, "E130.MirrorC", {"center": v(120.71, -231.04) * mm, "radius": 6.35 * mm});
            skCircle(sketch, "E131.MirrorC", {"center": v(120.71, -294.54) * mm, "radius": 6.35 * mm});
            skCircle(sketch, "E132.MirrorC", {"center": v(57.21, -294.54) * mm, "radius": 6.35 * mm});
            skCircle(sketch, "E133.MirrorC", {"center": v(57.21, -231.04) * mm, "radius": 6.35 * mm});
            skSolve(sketch);
        }
        {
            var Q0;
            Q0 = qSketchRegion(id + "F39", true);
            extrude(context, id + "F40", {"entities" : qUnion([Q0]), "depth" : 12.06 * mm, "offsetDistance" : 25.4 * mm});
        }
        {
            var Q0;
            Q0=makeQuery(id+"F20.opPattern","COPY",FACE,{"derivedFrom":makeQuery(id+"F19.opExtrude","CAP_FACE",FACE,{"disambiguationData":[OSD([sQuery(id+"F18.wireOp",EDGE,"E53"),sQuery(id+"F18.wireOp",EDGE,"E54"),sQuery(id+"F18.wireOp",EDGE,"E55"),sQuery(id+"F18.wireOp",EDGE,"E56.0"),sQuery(id+"F18.wireOp",EDGE,"E56.1"),sQuery(id+"F18.wireOp",EDGE,"E56.2"),sQuery(id+"F18.wireOp",EDGE,"E56.3"),sQuery(id+"F18.wireOp",EDGE,"E56.4"),sQuery(id+"F18.wireOp",EDGE,"E56.5"),sQuery(id+"F18.wireOp",EDGE,"E57"),sQuery(id+"F18.wireOp",EDGE,"E58"),sQuery(id+"F18.wireOp",EDGE,"E59"),sQuery(id+"F18.wireOp",EDGE,"E60"),sQuery(id+"F18.wireOp",EDGE,"E61"),sQuery(id+"F18.wireOp",EDGE,"E62.filletArc"),sQuery(id+"F18.wireOp",EDGE,"E63.filletArc"),sQuery(id+"F18.wireOp",EDGE,"E64"),sQuery(id+"F18.wireOp",EDGE,"E65"),sQuery(id+"F18.wireOp",EDGE,"E66"),sQuery(id+"F18.wireOp",EDGE,"E67"),sQuery(id+"F18.wireOp",EDGE,"E68"),sQuery(id+"F18.wireOp",EDGE,"E69.filletArc"),sQuery(id+"F18.wireOp",EDGE,"E70.filletArc"),sQuery(id+"F18.wireOp",EDGE,"E71.filletArc"),sQuery(id+"F18.wireOp",EDGE,"E72.filletArc"),sQuery(id+"F18.wireOp",EDGE,"E73.filletArc"),sQuery(id+"F18.wireOp",EDGE,"E74"),sQuery(id+"F18.wireOp",EDGE,"E75"),sQuery(id+"F18.wireOp",EDGE,"E76.trimOffspring"),sQuery(id+"F18.wireOp",EDGE,"E77.trimOffspring"),sQuery(id+"F18.wireOp",EDGE,"E78.filletArc"),sQuery(id+"F18.wireOp",EDGE,"E79.filletArc"),sQuery(id+"F18.wireOp",EDGE,"E80.filletArc"),sQuery(id+"F18.wireOp",EDGE,"E81.filletArc")])],"isStart":true}),"instanceName":"1"});
            var sketch = newSketch(context, id + "F41", { "sketchPlane" : qUnion([Q0])});
            skCircle(sketch, "E134", {"center": v(133.85, 41.9) * mm, "radius": 38.1 * mm});
            skPoint(sketch, "E135.0", {"position": v(82.8, 3.8) * mm});
            skPoint(sketch, "E136", {"position": v(133.85, 3.8) * mm});
            skSolve(sketch);
        }
        {
            var Q0;
            Q0 = qSketchRegion(id + "F41", true);
            extrude(context, id + "F42", {"entities" : qUnion([Q0]), "operationType" : NewBodyOperationType.ADD, "oppositeDirection" : true, "depth" : 3.43 * mm, "offsetDistance" : 25.4 * mm});
        }
    });
